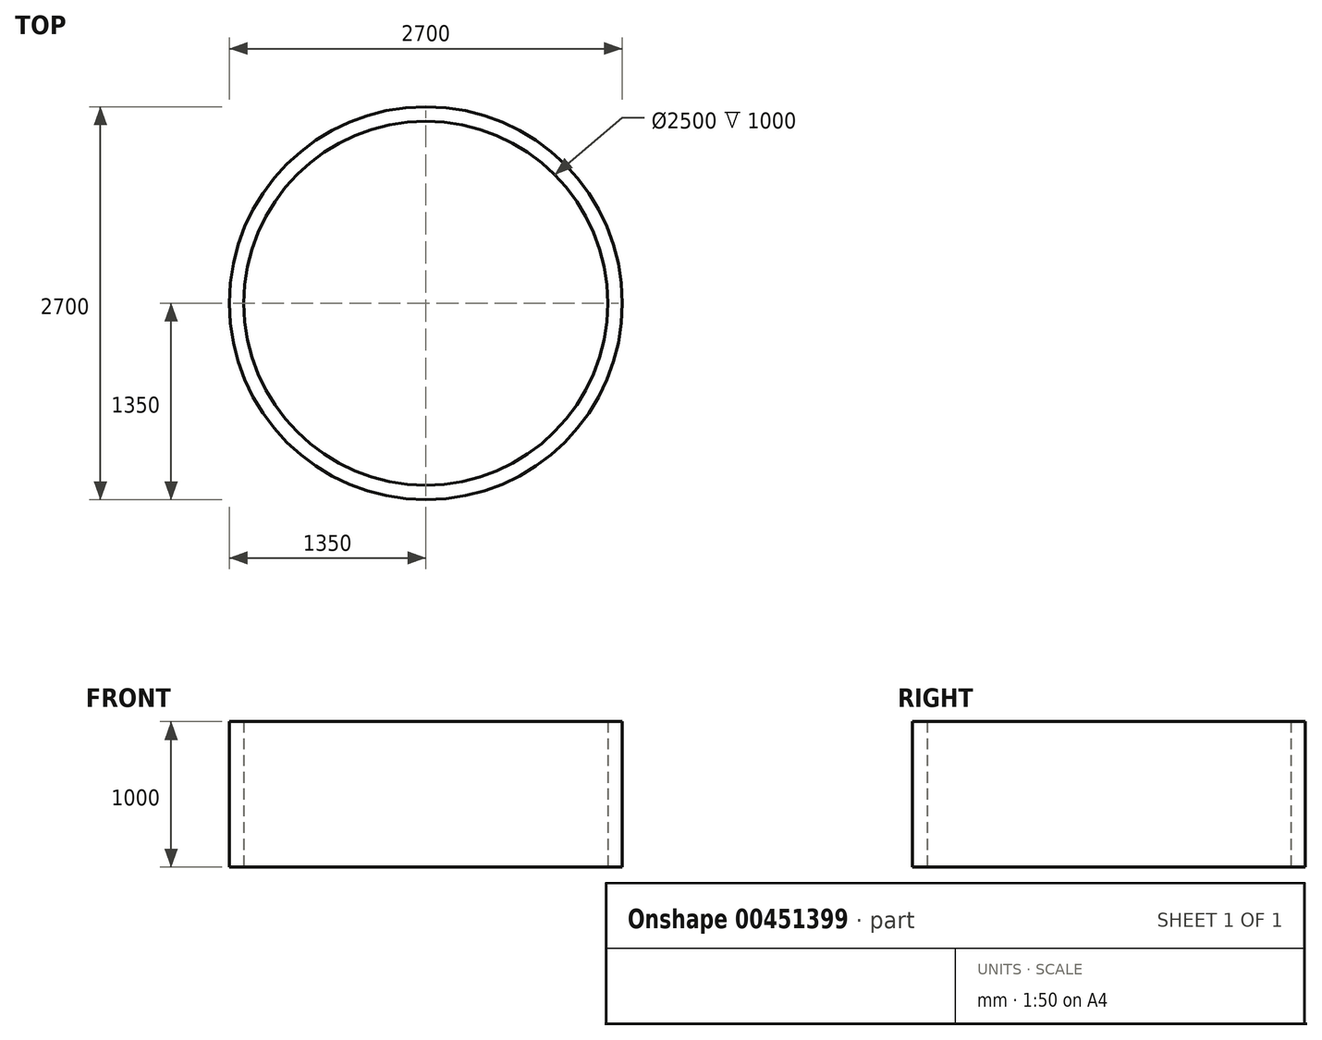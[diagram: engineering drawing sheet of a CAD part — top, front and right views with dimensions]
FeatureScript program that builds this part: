
annotation { "Feature Type Name" : "Feature", "Feature Type Description" : "" }
export const myFeature = defineFeature(function(context is Context, id is Id, definition is map)
    precondition{}
    {
        {
            var Q0;
            Q0=qCreatedBy(makeId("Top.planeOp"),FACE);
            var sketch = newSketch(context, id + "F0", { "sketchPlane" : qUnion([Q0])});
            skCircle(sketch, "E0", {"center": v(0, 0) * mm, "radius": 1250 * mm});
            skCircle(sketch, "E1", {"center": v(0, 0) * mm, "radius": 1350 * mm});
            skSolve(sketch);
        }
        {
            var Q0;
            Q0=makeQuery(id+"F0.imprint","IMPRINT",FACE,{"disambiguationData":[TD([[makeQuery(id+"F0.imprint","IMPRINT",EDGE,{"derivedFrom":sQuery(id+"F0.wireOp",EDGE,"E0")}),-1.0]])]});
            extrude(context, id + "F1", {"entities" : qUnion([Q0]), "endBound" : BoundingType.SYMMETRIC, "depth" : 1000 * mm, "offsetDistance" : 25 * mm});
        }
    });
